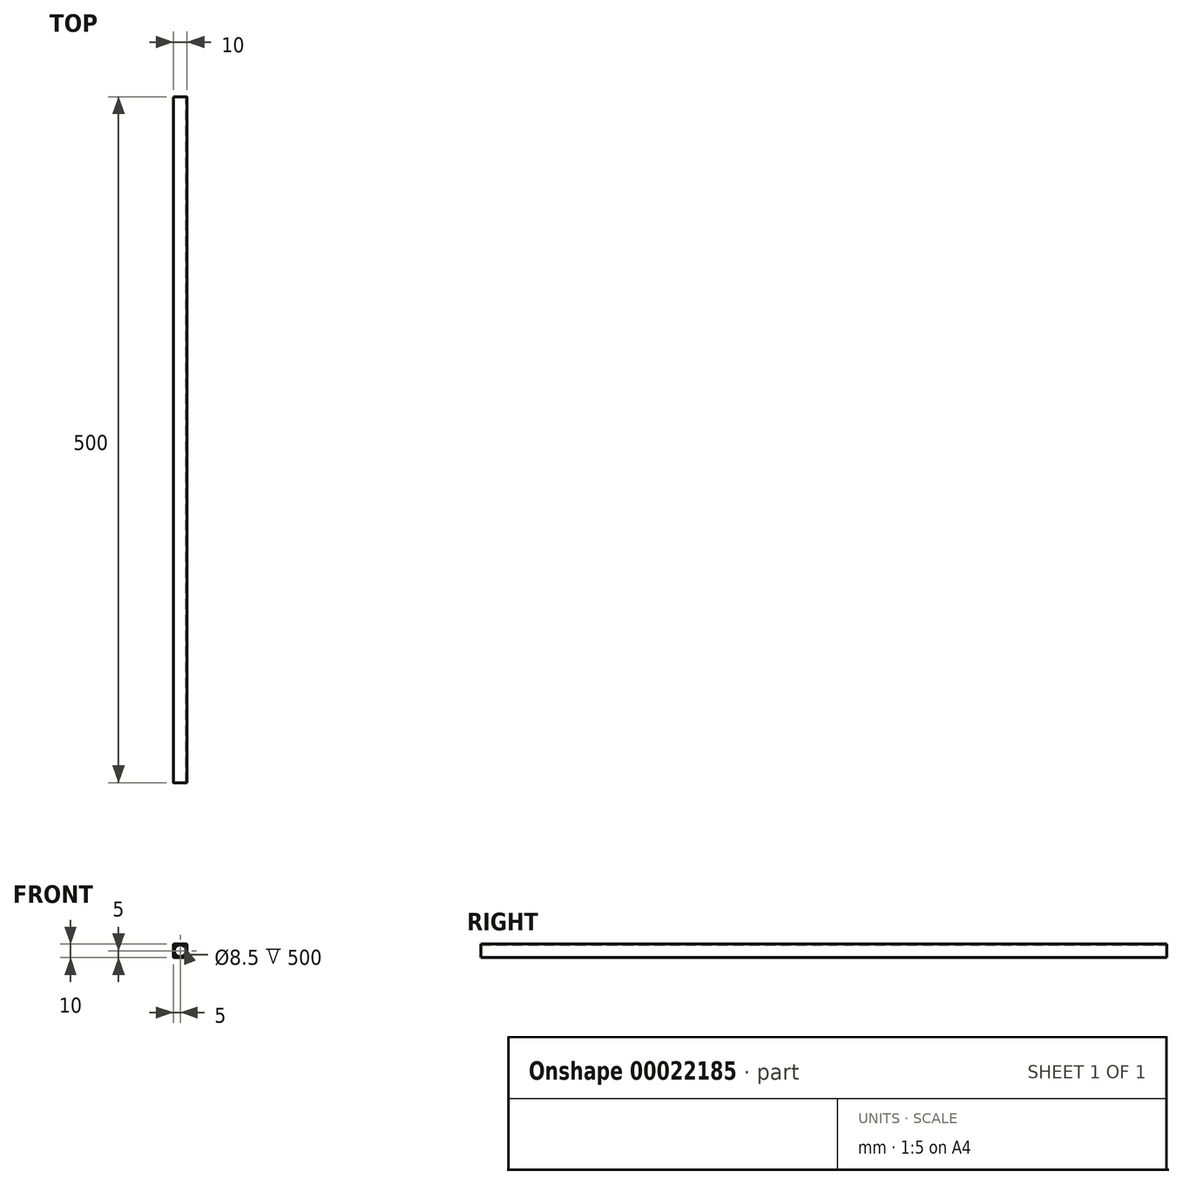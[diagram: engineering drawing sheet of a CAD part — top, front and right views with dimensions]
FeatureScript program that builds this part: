
annotation { "Feature Type Name" : "Feature", "Feature Type Description" : "" }
export const myFeature = defineFeature(function(context is Context, id is Id, definition is map)
    precondition{}
    {
        {
            var Q0;
            Q0=qCreatedBy(makeId("Front.planeOp"),FACE);
            var sketch = newSketch(context, id + "F0", { "sketchPlane" : qUnion([Q0])});
            skLineSegment(sketch, "E0.rect.bottom", {"start": v(4.5, -5) * mm, "end": v(-4.5, -5) * mm});
            skLineSegment(sketch, "E0.rect.top", {"start": v(4.5, 5) * mm, "end": v(-4.5, 5) * mm});
            skLineSegment(sketch, "E0.rect.left", {"start": v(5, -4.5) * mm, "end": v(5, 4.5) * mm});
            skLineSegment(sketch, "E0.rect.right", {"start": v(-5, -4.5) * mm, "end": v(-5, 4.5) * mm});
            skPoint(sketch, "E0.rect.middle", {"position": v(0, 0) * mm});
            skCircle(sketch, "E1", {"center": v(0, 0) * mm, "radius": 4.25 * mm});
            skPoint(sketch, "E2.visualSharp", {"position": v(5, 5) * mm});
            skArc(sketch, "E2.filletArc", {"start": v(5, 4.5) * mm, "mid": v(4.85, 4.85) * mm, "end": v(4.5, 5) * mm});
            skPoint(sketch, "E3.visualSharp", {"position": v(5, -5) * mm});
            skArc(sketch, "E3.filletArc", {"start": v(4.5, -5) * mm, "mid": v(4.85, -4.85) * mm, "end": v(5, -4.5) * mm});
            skPoint(sketch, "E4.visualSharp", {"position": v(-5, -5) * mm});
            skArc(sketch, "E4.filletArc", {"start": v(-5, -4.5) * mm, "mid": v(-4.85, -4.85) * mm, "end": v(-4.5, -5) * mm});
            skPoint(sketch, "E5.visualSharp", {"position": v(-5, 5) * mm});
            skArc(sketch, "E5.filletArc", {"start": v(-4.5, 5) * mm, "mid": v(-4.85, 4.85) * mm, "end": v(-5, 4.5) * mm});
            skSolve(sketch);
        }
        {
            var Q0;
            Q0=makeQuery(id+"F0.imprint","IMPRINT",FACE,{"disambiguationData":[TD([[makeQuery(id+"F0.imprint","IMPRINT",EDGE,{"derivedFrom":sQuery(id+"F0.wireOp",EDGE,"E0.rect.bottom")}),-1.0]])]});
            extrude(context, id + "F1", {"entities" : qUnion([Q0]), "depth" : 500 * mm});
        }
    });
